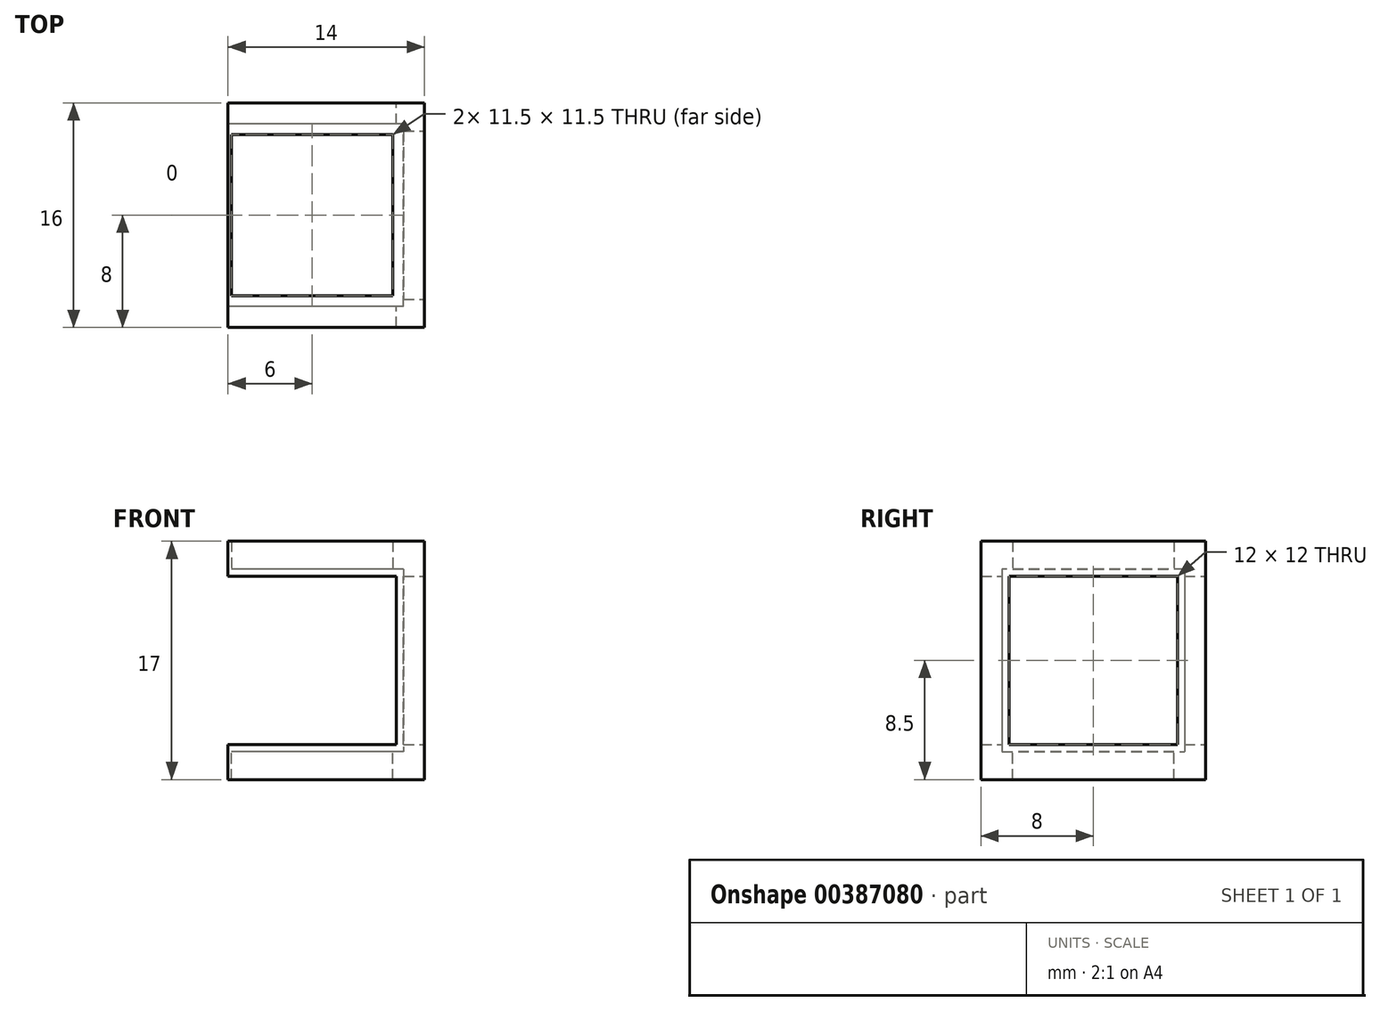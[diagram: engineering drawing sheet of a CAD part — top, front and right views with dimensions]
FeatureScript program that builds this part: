
annotation { "Feature Type Name" : "Feature", "Feature Type Description" : "" }
export const myFeature = defineFeature(function(context is Context, id is Id, definition is map)
    precondition{}
    {
        {
            var Q0;
            Q0=qCreatedBy(makeId("Top.planeOp"),FACE);
            var sketch = newSketch(context, id + "F0", { "sketchPlane" : qUnion([Q0])});
            skLineSegment(sketch, "E0.bottom", {"start": v(6.5, -6.5) * mm, "end": v(-6.5, -6.5) * mm});
            skLineSegment(sketch, "E0.top", {"start": v(6.5, 6.5) * mm, "end": v(-6.5, 6.5) * mm});
            skLineSegment(sketch, "E0.left", {"start": v(6.5, -6.5) * mm, "end": v(6.5, 6.5) * mm});
            skLineSegment(sketch, "E0.right", {"start": v(-6.5, -6.5) * mm, "end": v(-6.5, 6.5) * mm});
            skPoint(sketch, "E0.middle", {"position": v(0, 0) * mm});
            skLineSegment(sketch, "E1.bottom", {"start": v(8, -8) * mm, "end": v(-8, -8) * mm});
            skLineSegment(sketch, "E1.top", {"start": v(8, 8) * mm, "end": v(-8, 8) * mm});
            skLineSegment(sketch, "E1.left", {"start": v(8, -8) * mm, "end": v(8, 8) * mm});
            skLineSegment(sketch, "E1.right", {"start": v(-8, -8) * mm, "end": v(-8, 8) * mm});
            skSolve(sketch);
        }
        {
            var Q0;
            Q0 = qSketchRegion(id + "F0", true);
            extrude(context, id + "F1", {"entities" : qUnion([Q0]), "depth" : 13 * mm});
        }
        {
            var Q0;
            Q0=makeQuery(id+"F1.opExtrude","CAP_FACE",FACE,{"disambiguationData":[OSD([sQuery(id+"F0.wireOp",EDGE,"E0.bottom"),sQuery(id+"F0.wireOp",EDGE,"E0.top"),sQuery(id+"F0.wireOp",EDGE,"E0.left"),sQuery(id+"F0.wireOp",EDGE,"E0.right"),sQuery(id+"F0.wireOp",EDGE,"E1.bottom"),sQuery(id+"F0.wireOp",EDGE,"E1.top"),sQuery(id+"F0.wireOp",EDGE,"E1.left"),sQuery(id+"F0.wireOp",EDGE,"E1.right")])],"isStart":false});
            var sketch = newSketch(context, id + "F2", { "sketchPlane" : qUnion([Q0])});
            skLineSegment(sketch, "E2.bottom", {"start": v(8, -8) * mm, "end": v(-8, -8) * mm});
            skLineSegment(sketch, "E2.top", {"start": v(8, 8) * mm, "end": v(-8, 8) * mm});
            skLineSegment(sketch, "E2.left", {"start": v(8, -8) * mm, "end": v(8, 8) * mm});
            skLineSegment(sketch, "E2.right", {"start": v(-8, -8) * mm, "end": v(-8, 8) * mm});
            skPoint(sketch, "E2.middle", {"position": v(0, 0) * mm});
            skLineSegment(sketch, "E3.bottom", {"start": v(5.75, -5.75) * mm, "end": v(-5.75, -5.75) * mm});
            skLineSegment(sketch, "E3.top", {"start": v(5.75, 5.75) * mm, "end": v(-5.75, 5.75) * mm});
            skLineSegment(sketch, "E3.left", {"start": v(5.75, -5.75) * mm, "end": v(5.75, 5.75) * mm});
            skLineSegment(sketch, "E3.right", {"start": v(-5.75, -5.75) * mm, "end": v(-5.75, 5.75) * mm});
            skSolve(sketch);
        }
        {
            var Q0;
            Q0 = qSketchRegion(id + "F2", true);
            extrude(context, id + "F3", {"entities" : qUnion([Q0]), "operationType" : NewBodyOperationType.ADD, "depth" : 2 * mm});
        }
        {
            var Q0;
            Q0=makeQuery(id+"F1.opExtrude","CAP_FACE",FACE,{"disambiguationData":[OSD([sQuery(id+"F0.wireOp",EDGE,"E0.bottom"),sQuery(id+"F0.wireOp",EDGE,"E0.top"),sQuery(id+"F0.wireOp",EDGE,"E0.left"),sQuery(id+"F0.wireOp",EDGE,"E0.right"),sQuery(id+"F0.wireOp",EDGE,"E1.bottom"),sQuery(id+"F0.wireOp",EDGE,"E1.top"),sQuery(id+"F0.wireOp",EDGE,"E1.left"),sQuery(id+"F0.wireOp",EDGE,"E1.right")])],"isStart":true});
            var sketch = newSketch(context, id + "F4", { "sketchPlane" : qUnion([Q0])});
            skLineSegment(sketch, "E4.bottom", {"start": v(8, -8) * mm, "end": v(-8, -8) * mm});
            skLineSegment(sketch, "E4.top", {"start": v(8, 8) * mm, "end": v(-8, 8) * mm});
            skLineSegment(sketch, "E4.left", {"start": v(8, -8) * mm, "end": v(8, 8) * mm});
            skLineSegment(sketch, "E4.right", {"start": v(-8, -8) * mm, "end": v(-8, 8) * mm});
            skPoint(sketch, "E4.middle", {"position": v(0, 0) * mm});
            skLineSegment(sketch, "E5.bottom", {"start": v(5.75, -5.75) * mm, "end": v(-5.75, -5.75) * mm});
            skLineSegment(sketch, "E5.top", {"start": v(5.75, 5.75) * mm, "end": v(-5.75, 5.75) * mm});
            skLineSegment(sketch, "E5.left", {"start": v(5.75, -5.75) * mm, "end": v(5.75, 5.75) * mm});
            skLineSegment(sketch, "E5.right", {"start": v(-5.75, -5.75) * mm, "end": v(-5.75, 5.75) * mm});
            skSolve(sketch);
        }
        {
            var Q0;
            Q0 = qSketchRegion(id + "F4", true);
            extrude(context, id + "F5", {"entities" : qUnion([Q0]), "operationType" : NewBodyOperationType.ADD, "depth" : 2 * mm});
        }
        {
            var Q0;
            Q0=makeQuery(id+"F5.boolean.opBoolean","MERGE",FACE,{"derivedFrom":[makeQuery(id+"F3.boolean.opBoolean","MERGE",FACE,{"derivedFrom":[makeQuery(id+"F1.opExtrude","SWEPT_FACE",FACE,{"disambiguationData":[OSD([sQuery(id+"F0.wireOp",EDGE,"E1.top")])]}),makeQuery(id+"F3.opExtrude","SWEPT_FACE",FACE,{"disambiguationData":[OSD([sQuery(id+"F2.wireOp",EDGE,"E2.top")])]})]}),makeQuery(id+"F5.opExtrude","SWEPT_FACE",FACE,{"disambiguationData":[OSD([sQuery(id+"F4.wireOp",EDGE,"E4.bottom")])]})]});
            var sketch = newSketch(context, id + "F6", { "sketchPlane" : qUnion([Q0])});
            skPoint(sketch, "E6", {"position": v(0, 6.5) * mm});
            skLineSegment(sketch, "E7.bottom", {"start": v(6, 0.5) * mm, "end": v(-6, 0.5) * mm});
            skLineSegment(sketch, "E7.top", {"start": v(6, 12.5) * mm, "end": v(-6, 12.5) * mm});
            skLineSegment(sketch, "E7.left", {"start": v(6, 0.5) * mm, "end": v(6, 12.5) * mm});
            skLineSegment(sketch, "E7.right", {"start": v(-6, 0.5) * mm, "end": v(-6, 12.5) * mm});
            skSolve(sketch);
        }
        {
            var Q0;
            Q0=makeQuery(id+"F6.imprint","IMPRINT",FACE,{"disambiguationData":[TD([[makeQuery(id+"F6.imprint","IMPRINT",EDGE,{"derivedFrom":sQuery(id+"F6.wireOp",EDGE,"E7.bottom")}),-1.0]])]});
            extrude(context, id + "F7", {"entities" : qUnion([Q0]), "operationType" : NewBodyOperationType.REMOVE, "endBound" : BoundingType.THROUGH_ALL, "oppositeDirection" : true, "depth" : 25 * mm});
        }
        {
            var Q0;
            Q0=makeQuery(id+"F5.boolean.opBoolean","MERGE",FACE,{"derivedFrom":[makeQuery(id+"F3.boolean.opBoolean","MERGE",FACE,{"derivedFrom":[makeQuery(id+"F1.opExtrude","SWEPT_FACE",FACE,{"disambiguationData":[OSD([sQuery(id+"F0.wireOp",EDGE,"E1.left")])]}),makeQuery(id+"F3.opExtrude","SWEPT_FACE",FACE,{"disambiguationData":[OSD([sQuery(id+"F2.wireOp",EDGE,"E2.left")])]})]}),makeQuery(id+"F5.opExtrude","SWEPT_FACE",FACE,{"disambiguationData":[OSD([sQuery(id+"F4.wireOp",EDGE,"E4.left")])]})]});
            var sketch = newSketch(context, id + "F8", { "sketchPlane" : qUnion([Q0])});
            skPoint(sketch, "E8", {"position": v(0, 6.5) * mm});
            skLineSegment(sketch, "E9.bottom", {"start": v(6, 0.5) * mm, "end": v(-6, 0.5) * mm});
            skLineSegment(sketch, "E9.top", {"start": v(6, 12.5) * mm, "end": v(-6, 12.5) * mm});
            skLineSegment(sketch, "E9.left", {"start": v(6, 0.5) * mm, "end": v(6, 12.5) * mm});
            skLineSegment(sketch, "E9.right", {"start": v(-6, 0.5) * mm, "end": v(-6, 12.5) * mm});
            skSolve(sketch);
        }
        {
            var Q0;
            Q0 = qSketchRegion(id + "F8", true);
            extrude(context, id + "F9", {"entities" : qUnion([Q0]), "operationType" : NewBodyOperationType.REMOVE, "endBound" : BoundingType.UP_TO_NEXT, "oppositeDirection" : true, "depth" : 25 * mm});
        }
        {
            var Q0;
            Q0=makeQuery(id+"F5.boolean.opBoolean","MERGE",FACE,{"derivedFrom":[makeQuery(id+"F3.boolean.opBoolean","MERGE",FACE,{"derivedFrom":[makeQuery(id+"F1.opExtrude","SWEPT_FACE",FACE,{"disambiguationData":[OSD([sQuery(id+"F0.wireOp",EDGE,"E1.right")])]}),makeQuery(id+"F3.opExtrude","SWEPT_FACE",FACE,{"disambiguationData":[OSD([sQuery(id+"F2.wireOp",EDGE,"E2.right")])]})]}),makeQuery(id+"F5.opExtrude","SWEPT_FACE",FACE,{"disambiguationData":[OSD([sQuery(id+"F4.wireOp",EDGE,"E4.right")])]})]});
            var sketch = newSketch(context, id + "F10", { "sketchPlane" : qUnion([Q0])});
            skLineSegment(sketch, "E10.bottom", {"start": v(-8, 15) * mm, "end": v(8, 15) * mm});
            skLineSegment(sketch, "E10.top", {"start": v(-8, -2) * mm, "end": v(8, -2) * mm});
            skLineSegment(sketch, "E10.left", {"start": v(-8, 15) * mm, "end": v(-8, -2) * mm});
            skLineSegment(sketch, "E10.right", {"start": v(8, 15) * mm, "end": v(8, -2) * mm});
            skSolve(sketch);
        }
        {
            var Q0;
            Q0 = qSketchRegion(id + "F10", true);
            extrude(context, id + "F11", {"entities" : qUnion([Q0]), "operationType" : NewBodyOperationType.REMOVE, "oppositeDirection" : true, "depth" : 2 * mm});
        }
    });
